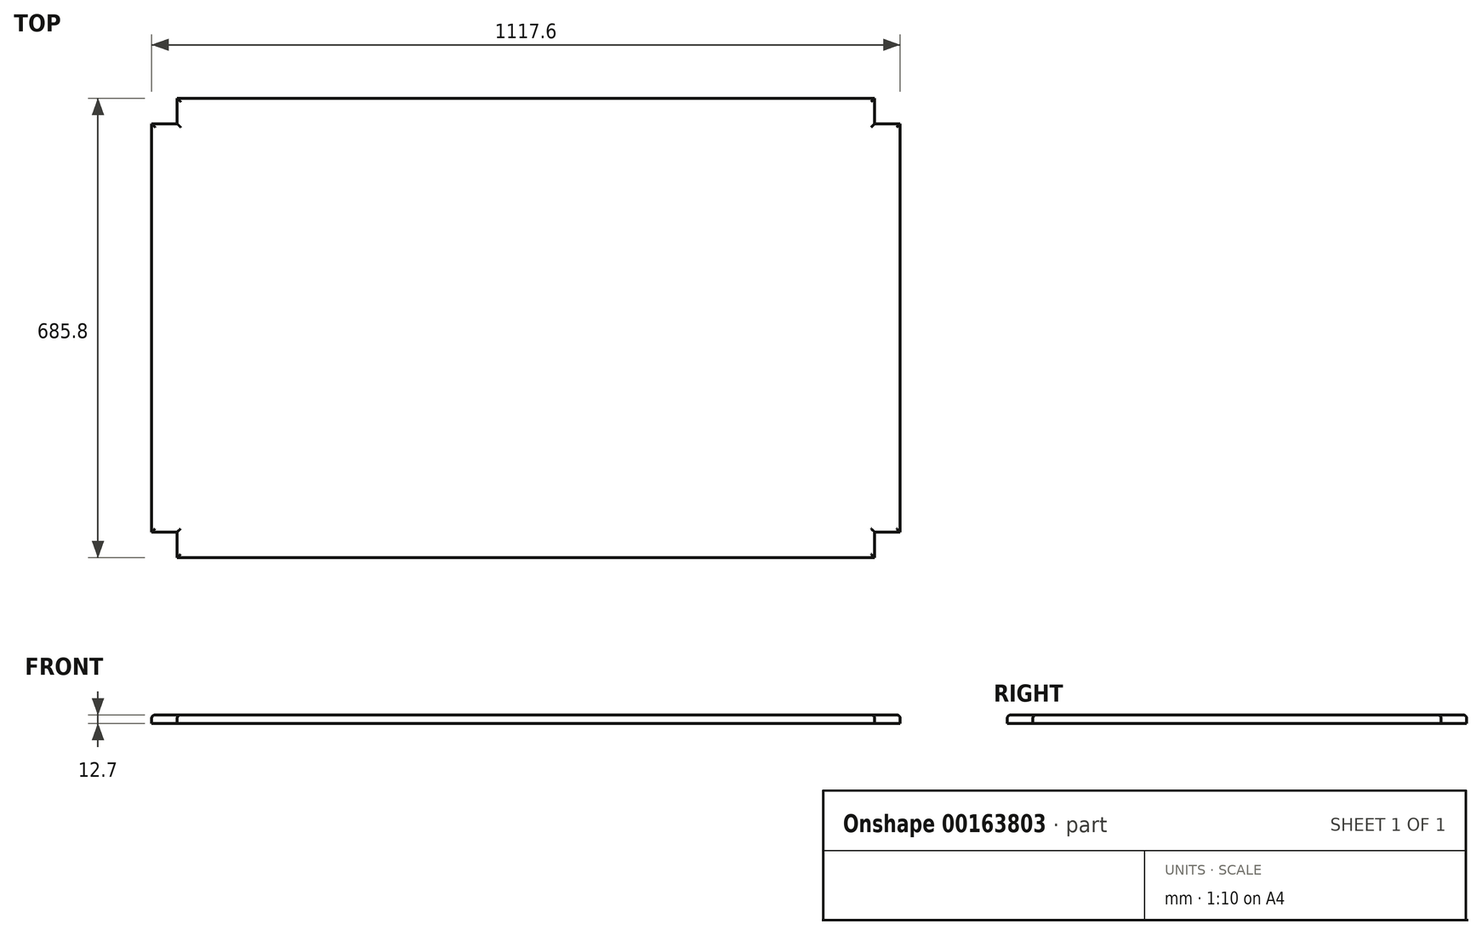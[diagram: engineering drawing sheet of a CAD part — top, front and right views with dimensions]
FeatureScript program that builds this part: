
annotation { "Feature Type Name" : "Feature", "Feature Type Description" : "" }
export const myFeature = defineFeature(function(context is Context, id is Id, definition is map)
    precondition{}
    {
        {
            var Q0;
            Q0=qCreatedBy(makeId("Top.planeOp"),FACE);
            var sketch = newSketch(context, id + "F0", { "sketchPlane" : qUnion([Q0])});
            skLineSegment(sketch, "E0.bottom", {"start": v(520.7, -342.9) * mm, "end": v(-520.7, -342.9) * mm});
            skLineSegment(sketch, "E0.top", {"start": v(520.7, 342.9) * mm, "end": v(-520.7, 342.9) * mm});
            skPoint(sketch, "E0.middle", {"position": v(0, 0) * mm});
            skLineSegment(sketch, "E1.trimOffspring", {"start": v(-558.8, -304.8) * mm, "end": v(-558.8, 304.8) * mm});
            skLineSegment(sketch, "E2", {"start": v(0, 0) * mm, "end": v(0, 342.9) * mm, "construction": true});
            skLineSegment(sketch, "E3", {"start": v(558.8, -304.8) * mm, "end": v(558.8, 304.8) * mm});
            skLineSegment(sketch, "E4.top", {"start": v(-558.8, 304.8) * mm, "end": v(-520.7, 304.8) * mm});
            skLineSegment(sketch, "E4.right", {"start": v(-520.7, 342.9) * mm, "end": v(-520.7, 304.8) * mm});
            skLineSegment(sketch, "E5.MirrorCS", {"start": v(520.7, 342.9) * mm, "end": v(520.7, 304.8) * mm});
            skLineSegment(sketch, "E6.MirrorCS", {"start": v(558.8, 304.8) * mm, "end": v(520.7, 304.8) * mm});
            skLineSegment(sketch, "E7", {"start": v(0, 0) * mm, "end": v(558.8, 0) * mm, "construction": true});
            skLineSegment(sketch, "E8.MirrorCS", {"start": v(-558.8, -304.8) * mm, "end": v(-520.7, -304.8) * mm});
            skLineSegment(sketch, "E9.MirrorCS", {"start": v(-520.7, -342.9) * mm, "end": v(-520.7, -304.8) * mm});
            skLineSegment(sketch, "E10.MirrorCS", {"start": v(520.7, -342.9) * mm, "end": v(520.7, -304.8) * mm});
            skLineSegment(sketch, "E11.MirrorCS", {"start": v(558.8, -304.8) * mm, "end": v(520.7, -304.8) * mm});
            skSolve(sketch);
        }
        {
            var Q0;
            Q0=qSketchRegion(id+"F0",true);
            extrude(context, id + "F1", {"entities" : qUnion([Q0]), "depth" : 12.7 * mm});
        }
        {
            var Q0;
            Q0=makeQuery(id+"F1.opExtrude","CAP_FACE",FACE,{"disambiguationData":[OSD([sQuery(id+"F0.wireOp",EDGE,"E0.bottom"),sQuery(id+"F0.wireOp",EDGE,"E0.top"),sQuery(id+"F0.wireOp",EDGE,"E0.left"),sQuery(id+"F0.wireOp",EDGE,"E0.right"),sQuery(id+"F0.wireOp",EDGE,"b15ae54a-3f8c-4f60-8baa-cd31eb437c6e.filletArc"),sQuery(id+"F0.wireOp",EDGE,"aa749b1a-4f62-40e5-a9dd-a47ec50e650c.filletArc"),sQuery(id+"F0.wireOp",EDGE,"2b33ca63-df12-433b-986b-ef48bfc9de00.filletArc"),sQuery(id+"F0.wireOp",EDGE,"b19e8cbf-3efd-47e7-9b03-fc77b71e0aba.filletArc")])],"isStart":false});
            fillet(context, id + "F2", {"entities" : qUnion([Q0]), "radius" : 5.08 * mm, "tangentPropagation" : true, "allowEdgeOverflow" : false});
        }
    });
